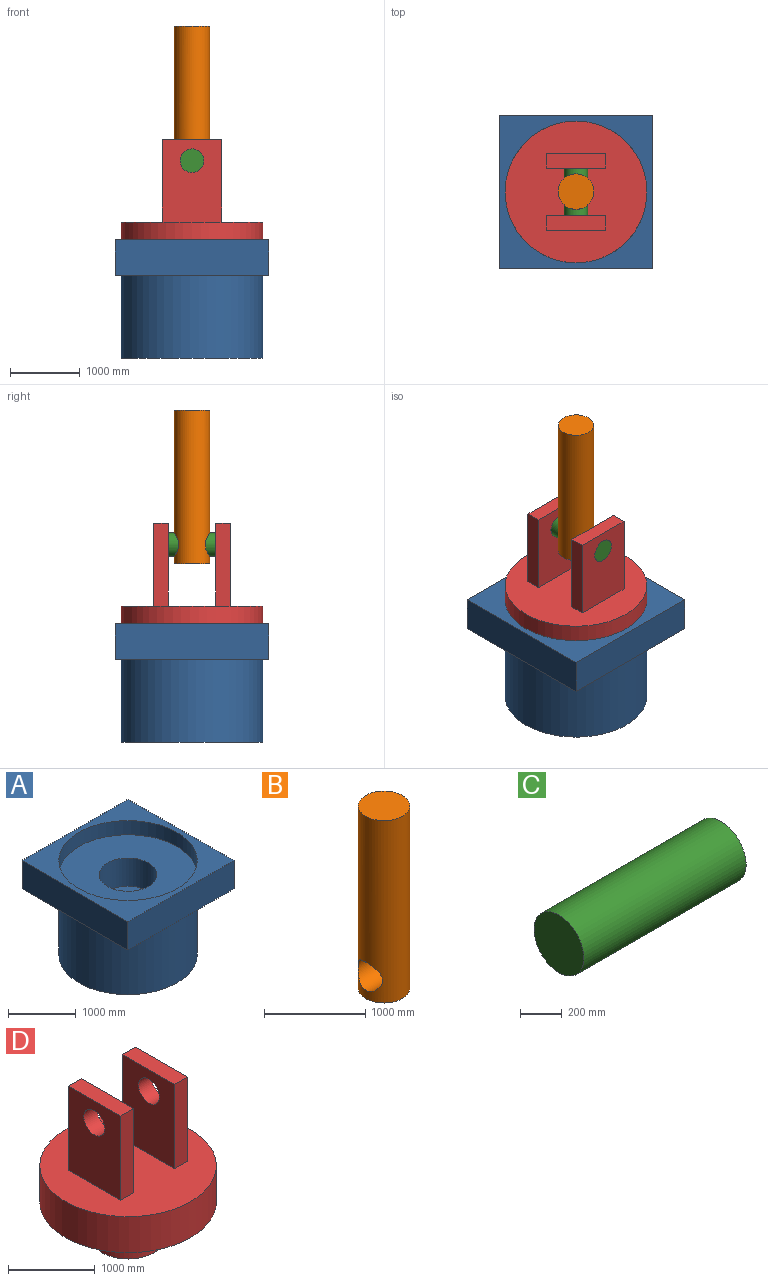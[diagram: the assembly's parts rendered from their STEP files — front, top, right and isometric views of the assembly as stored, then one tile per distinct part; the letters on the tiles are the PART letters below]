
ASSEMBLY  parts=4 mates=3
PART A: 12 faces, bbox 2210x2210x1700 mm
  f0: plane 2210x510mm, normal (1,0,0), area 1127100mm2, adj f1,f3,f4,f5
  f1: plane 2210x510mm, normal (0,1,0), area 1127100mm2, adj f0,f2,f4,f5
  f2: plane 2210x510mm, normal (-1,0,0), area 1127100mm2, adj f1,f3,f4,f5
  f3: plane 2210x510mm, normal (0,-1,0), area 1127100mm2, adj f0,f2,f4,f5
  f4: plane 2210x2210mm, normal (0,0,1), area 1615587mm2, adj f0,f1,f2,f3,f8
  f5: plane 2210x2210mm, normal (0,0,-1), area 1615587mm2, adj f0,f1,f2,f3,f6
  f6: cylinder r=1020mm len=2040mm, axis (0,0,1), area 7626530.3mm2, adj f5,f7
  f7: plane 2040x2040mm, normal (0,0,-1), area 3268513mm2, adj f6
  f8: cylinder r=1020mm len=2040mm, axis (0,0,-1), area 1634256.5mm2, adj f4,f9
  f9: plane 2040x2040mm, normal (0,0,1), area 2701062.8mm2, adj f8,f10
  f10: cylinder r=425mm len=850mm, axis (0,0,1), area 1361880.4mm2, adj f9,f11
  f11: plane 850x850mm, normal (0,0,1), area 567450.2mm2, adj f10
PART B: 4 faces, bbox 510x510x2210 mm
  f0: cylinder r=255mm len=2210mm, axis (0,0,-1), area 3347001.8mm2, adj f1,f2,f3
  f1: plane 510x510mm, normal (0,0,1), area 204282.1mm2, adj f0
  f2: plane 510x510mm, normal (0,0,-1), area 204282.1mm2, adj f0
  f3: cylinder r=170mm len=510mm, axis (1,0,0), area 477917.8mm2, adj f0
PART C: 3 faces, bbox 1105x340x340 mm
  f0: plane 340x340mm, normal (-1,0,0), area 90792mm2, adj f1
  f1: cylinder r=170mm len=1105mm, axis (1,0,0), area 1180296.4mm2, adj f0,f2
  f2: plane 340x340mm, normal (1,0,0), area 90792mm2, adj f1
PART D: 17 faces, bbox 2040x2040x2210 mm
  f0: plane 2040x2040mm, normal (0,0,1), area 2907263mm2, adj f1,f3,f4,f5,f6,f8,f9,f10
  f1: cylinder r=1020mm len=2040mm, axis (0,0,-1), area 3268513mm2, adj f0,f2
  f2: plane 2040x2040mm, normal (0,0,-1), area 2701062.8mm2, adj f1,f13
  f3: plane 1190x850mm, normal (-1,0,0), area 920708mm2, adj f0,f4,f6,f7,f16
  f4: plane 1190x212.5mm, normal (0,-1,0), area 252875mm2, adj f0,f3,f5,f7
  f5: plane 1190x850mm, normal (1,0,0), area 920708mm2, adj f0,f4,f6,f7,f16
  f6: plane 1190x212.5mm, normal (0,1,0), area 252875mm2, adj f0,f3,f5,f7
  f7: plane 850x212.5mm, normal (0,0,1), area 180625mm2, adj f3,f4,f5,f6
  f8: plane 1190x212.5mm, normal (0,1,0), area 252875mm2, adj f0,f9,f11,f12
  f9: plane 1190x850mm, normal (-1,0,0), area 920708mm2, adj f0,f8,f10,f12,f15
  f10: plane 1190x212.5mm, normal (0,-1,0), area 252875mm2, adj f0,f9,f11,f12
  f11: plane 1190x850mm, normal (1,0,0), area 920708mm2, adj f0,f8,f10,f12,f15
  f12: plane 850x212.5mm, normal (0,0,1), area 180625mm2, adj f8,f9,f10,f11
  f13: cylinder r=425mm len=850mm, axis (0,0,1), area 1361880.4mm2, adj f2,f14
  f14: plane 850x850mm, normal (0,0,-1), area 567450.2mm2, adj f13
  f15: cylinder r=170mm len=340mm, axis (1,0,0), area 226980.1mm2, adj f9,f11
  f16: cylinder r=170mm len=340mm, axis (1,0,0), area 226980.1mm2, adj f3,f5
PLACE A at identity fixed
PLACE B rot(axis=(0,0,-1),90deg) t=(0,0.01,0)mm
PLACE C rot(axis=(0,0,-1),90deg) t=(0,0,0)mm
PLACE D rot(axis=(0,0,-1),90deg) t=(0,0,0)mm
MATE revolute C.f1 <-> D.f15  axis (0,-1,0) through (0,-552.5,1649)mm
MATE fastened B.f3 <-> C.f1  axis (0,-1,0) through (0,0,1649)mm
MATE revolute D.f1 <-> A.f6  axis (0,0,-1) through (0,0,-255)mm
